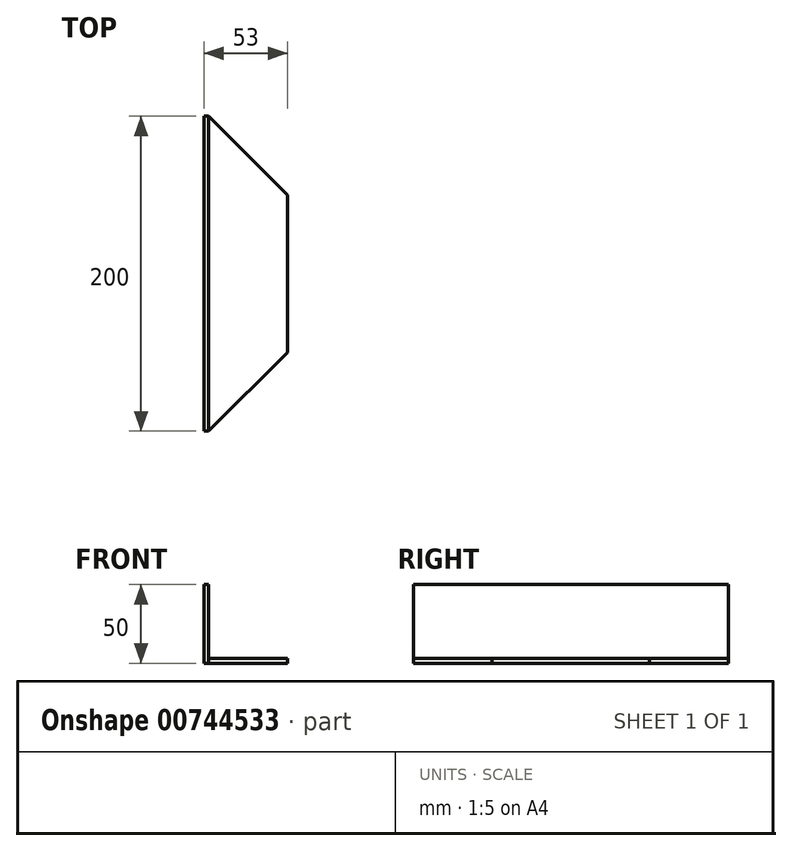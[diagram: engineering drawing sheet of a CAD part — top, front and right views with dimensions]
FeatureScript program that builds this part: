
annotation { "Feature Type Name" : "Feature", "Feature Type Description" : "" }
export const myFeature = defineFeature(function(context is Context, id is Id, definition is map)
    precondition{}
    {
        {
            var Q0;
            Q0=qCreatedBy(makeId("Top.planeOp"),FACE);
            var sketch = newSketch(context, id + "F0", { "sketchPlane" : qUnion([Q0])});
            skLineSegment(sketch, "E0.left", {"start": v(-123.6, 106.56) * mm, "end": v(-123.6, -93.44) * mm});
            skLineSegment(sketch, "E1.left", {"start": v(-73.6, 56.56) * mm, "end": v(-73.6, -43.44) * mm});
            skLineSegment(sketch, "E2", {"start": v(-73.6, 56.56) * mm, "end": v(-123.6, 106.56) * mm});
            skLineSegment(sketch, "E3", {"start": v(-73.6, -43.44) * mm, "end": v(-123.6, -93.44) * mm});
            skLineSegment(sketch, "E4", {"start": v(-123.6, 106.56) * mm, "end": v(-126.6, 106.56) * mm});
            skLineSegment(sketch, "E5", {"start": v(-123.6, -93.44) * mm, "end": v(-126.6, -93.44) * mm});
            skLineSegment(sketch, "E6", {"start": v(-126.6, -93.44) * mm, "end": v(-126.6, 106.56) * mm});
            skSolve(sketch);
        }
        {
            var Q0;
            Q0=makeQuery(id+"F0.imprint","IMPRINT",FACE,{"disambiguationData":[TD([[makeQuery(id+"F0.imprint","IMPRINT",EDGE,{"derivedFrom":sQuery(id+"F0.wireOp",EDGE,"E0.left")}),-1.0]])]});
            extrude(context, id + "F1", {"entities" : qUnion([Q0]), "depth" : 50 * mm, "offsetDistance" : 25 * mm});
        }
        {
            var Q0;
            Q0=makeQuery(id+"F0.imprint","IMPRINT",FACE,{"disambiguationData":[TD([[makeQuery(id+"F0.imprint","IMPRINT",EDGE,{"derivedFrom":sQuery(id+"F0.wireOp",EDGE,"E0.left")}),1.0]])]});
            extrude(context, id + "F2", {"entities" : qUnion([Q0]), "operationType" : NewBodyOperationType.ADD, "depth" : 3 * mm, "offsetDistance" : 25 * mm});
        }
    });
